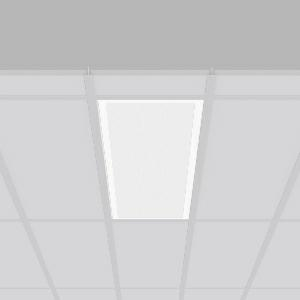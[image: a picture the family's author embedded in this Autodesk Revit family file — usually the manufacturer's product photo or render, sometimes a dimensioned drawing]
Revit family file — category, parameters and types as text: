
# Revit family: sidelite_eco_672374_002_4821
name_source: partatom
category: Lighting Fixtures
units: mm (PartAtom-declared; Revit-internal decimal feet)

## family parameters
Cut with Voids When Loaded = No
Host = Face
Light Source = No
Part Type = Normal
Room Calculation Point = No
Round Connector Dimension = Use Diameter
Shared = No

## types (1)
- SIDELITE ECO (1 x LED Modul 830, 3150 lm, 3000)
    Apparent Load = 29 VA
    CIE Flux Codes = 60 87 97 100 100
    Color Rendering = 80
    Color Temperature = 3000
    Default Elevation = 1800 mm
    Description = Series: SIDELITE ECO
Highly economical recessed luminaire with progressive LED technology. For escape route illumination. Frame made of aluminium, powder-coated. Diffuser plastic microprismatic. Lightguide and diffuser made of non-yellowing plastic (PMMA). Lateral light emission (RZB SIDELITE technology) for homogeneous light distribution. External driver. Self-contained system with automatic self-test. External driver with simple plug-in locking system. Extended connection cable (1.90 m). 
Colour: white
Length: 1245 mm
Width: 308 mm
Cut-out length: 1220 mm
Cut-out width: 285 mm
Recess height: 160 mm
Luminaire: recess height: 40 mm
Weight: 4.7 kg
Operating mode: maintained power mode
Duration time: 3 h
Lamp: LED
Socket: without socket
Colour temperature: 3000K
Colour rendering index (CRI): 80
System power: 29 W
Rated luminous flux: 3150 lm
Luminous flux, emergency: 460 lm
System power, emergency: -
Control gear: Regulated power supply
Protection class: I
Type of protection: IP 40
    Height = 0 mm  [stored 0 ft]
    Lamp = 1 x LED Modul 830
    Lamp Light Flux = 3150 lm
    Lamp count = 1
    Length = 1245 mm
    Lifetime = 50000 h
    Luminous efficacy = 109 lm/W
    Manufacturer = RZB
    ModVariant = No
    Model = 672374.002
    Mounting Place = Ceiling
    Mounting Type = Recessed
    Number of Poles = 1
    OnlyDefault = Yes
    Power Factor = 1
    Product Name = SIDELITE ECO
    Product group = Recessed modular luminaires
    ProductGroupID = 406
    Protection Class = Protection class I
    Protection Degree = IP 40
    RLX_Detail_Level = 1
    RLX_Emergency_Light_Flux = 460 lm
    RLX_Emergency_Type = 3
    RLX_Emergency_Type_DB = Yes
    RlxData = <blob elided: 34169 chars, md5=0bb9c70b>
    Socket = socket
    Standby Power = 0 W
    System Light Flux = 3150 lm
    System Power = 29 W
    Type Comments = Product without accessories
    Type Image = 312368.002.jpg
    URL = http://relux.com
    VarID = ---
    Voltage = 230 V
    Voltage Range = 220-240 V
    Weight = 0.00 kg
    Width = 308 mm

note: [stored X ft] marks values corroborated as IEEE doubles in the binary element streams (Revit-internal decimal feet)

## geometry (parser evidence)
native form markers: Blend x4, Sweep x11
no freeform markers — native parametric forms only
